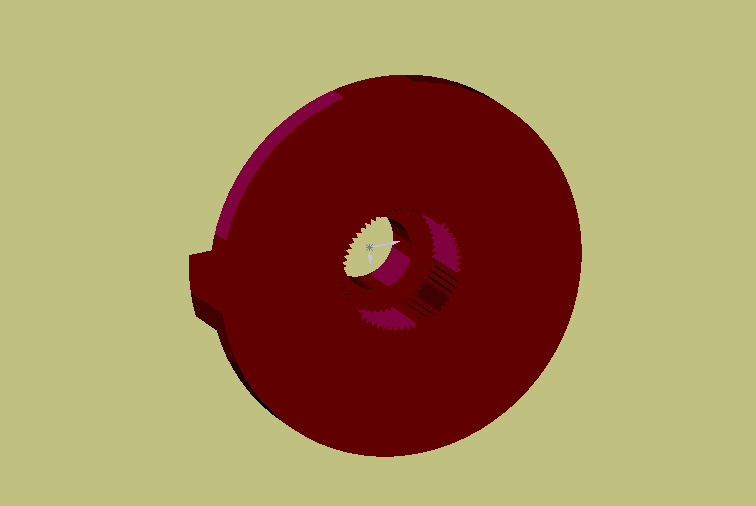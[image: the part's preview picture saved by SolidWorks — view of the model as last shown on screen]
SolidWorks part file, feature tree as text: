
SOLIDWORKS PART (.sldprt)
format: sldprt  version: not decoded by parser v0  size: 240,128 bytes
history: native  units: mm
features: sketch x6, extrude x4, plane x3, cut_extrude x2, material x1 (+8 scaffold rows collapsed)
feature tree (24):
  scaffold x8  (default folders/planes/origin — collapsed)
  material  "Matériau <non spécifié>"
  plane  "Plane1"
  plane  "Plane2"
  plane  "Plane3"
  sketch  "Esquisse1"  dims[c1.D1=6.0mm c1.D3=5.5mm c1.D2=~3.162278mm c2.D2=6.0deg c2.D1=2.75mm c2.D3=3.0mm c2.D4=2.75mm]
  sketch  "Esquisse2"  dims[D1=12.0mm D3=9.0mm D2=3.0mm]
  extrude  "Base-Extrusion"  Depth=2.75mm
  sketch  "Esquisse3"
  extrude  "Boss.-Extru.1"  Depth=1.5mm
  cut_extrude  "Enlèv. mat.-Extru.2"  [1 undecoded]
  sketch  "Esquisse5"  dims[D1=8.0mm D2=~2.491048mm]
  extrude  "Boss.-Extru.2"  Depth=1mm
  sketch  "Esquisse6"  dims[D1=5.0mm]
  extrude  "Boss.-Extru.3"  Depth=1.5mm
  sketch  "Esquisse7"  dims[D1=3.5mm]
  cut_extrude  "Enlèv. mat.-Extru.3"  [1 undecoded]
decode coverage: 9 of 12 modeling features carry decoded parameters
note: ~ marks probable driven/reference dimensions
note: 2 parameter values undecoded
note: suppression state not decoded; provenance and decode notes live in map.json
